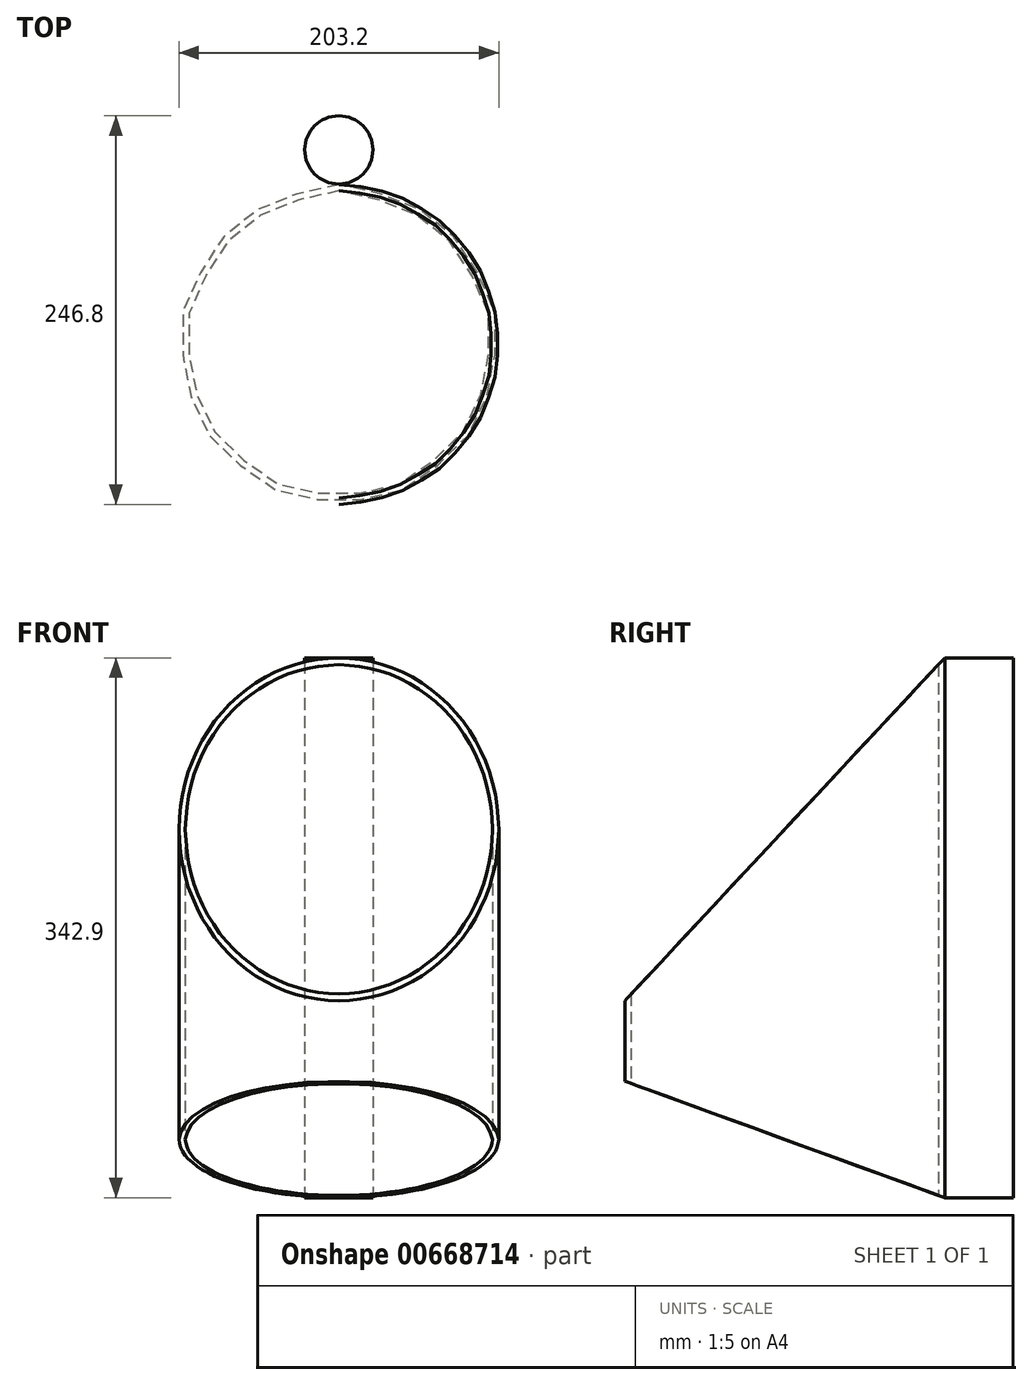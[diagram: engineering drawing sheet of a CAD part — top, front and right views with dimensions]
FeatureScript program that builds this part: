
annotation { "Feature Type Name" : "Feature", "Feature Type Description" : "" }
export const myFeature = defineFeature(function(context is Context, id is Id, definition is map)
    precondition{}
    {
        {
            var Q0;
            Q0=qCreatedBy(makeId("Top.planeOp"),FACE);
            var sketch = newSketch(context, id + "F0", { "sketchPlane" : qUnion([Q0])});
            skCircle(sketch, "E0", {"center": v(0, 0) * mm, "radius": 101.6 * mm});
            skCircle(sketch, "E1.0", {"center": v(0, 0) * mm, "radius": 97.54 * mm});
            skSolve(sketch);
        }
        {
            var Q0;
            Q0=qSketchRegion(id+"F0",true);
            extrude(context, id + "F1", {"entities" : qUnion([Q0]), "depth" : 342.9 * mm, "offsetDistance" : 25.4 * mm});
        }
        {
            var Q0;
            Q0=qCreatedBy(makeId("Right.planeOp"),FACE);
            var sketch = newSketch(context, id + "F2", { "sketchPlane" : qUnion([Q0])});
            skLineSegment(sketch, "E2.bottom", {"start": v(101.6, 342.9) * mm, "end": v(-101.6, 342.9) * mm});
            skLineSegment(sketch, "E2.right", {"start": v(-101.6, 342.9) * mm, "end": v(-101.6, 125) * mm});
            skPoint(sketch, "E2.middle", {"position": v(0, 233.95) * mm});
            skLineSegment(sketch, "E3.bottom", {"start": v(101.6, 0) * mm, "end": v(-101.6, 0) * mm});
            skLineSegment(sketch, "E3.right", {"start": v(-101.6, 0) * mm, "end": v(-101.6, 73.96) * mm});
            skPoint(sketch, "E3.middle", {"position": v(0, 36.98) * mm});
            skLineSegment(sketch, "E4", {"start": v(-101.6, 125) * mm, "end": v(101.6, 342.9) * mm});
            skPoint(sketch, "E2.top.start.orphan", {"position": v(101.6, 125) * mm});
            skLineSegment(sketch, "E5", {"start": v(-101.6, 73.96) * mm, "end": v(101.6, 0) * mm});
            skPoint(sketch, "E3.left.end.orphan", {"position": v(101.6, 73.96) * mm});
            skLineSegment(sketch, "E6", {"start": v(-101.6, 73.96) * mm, "end": v(101.6, 73.96) * mm});
            skSolve(sketch);
        }
        {
            var Q0;
            Q0=qSketchRegion(id+"F2",true);
            extrude(context, id + "F3", {"entities" : qUnion([Q0]), "operationType" : NewBodyOperationType.REMOVE, "endBound" : BoundingType.THROUGH_ALL, "depth" : 25.4 * mm, "hasSecondDirection" : true, "secondDirectionBound" : SecondDirectionBoundingType.THROUGH_ALL, "secondDirectionOppositeDirection" : true, "secondDirectionDepth" : 25.4 * mm});
        }
        {
            var Q0;
            Q0=qCreatedBy(makeId("Top.planeOp"),FACE);
            var sketch = newSketch(context, id + "F4", { "sketchPlane" : qUnion([Q0])});
            skCircle(sketch, "E7", {"center": v(0, 123.54) * mm, "radius": 21.66 * mm});
            skSolve(sketch);
        }
        {
            var Q0;
            Q0=qSketchRegion(id+"F4",true);
            extrude(context, id + "F5", {"entities" : qUnion([Q0]), "depth" : 342.9 * mm, "offsetDistance" : 25.4 * mm});
        }
    });
